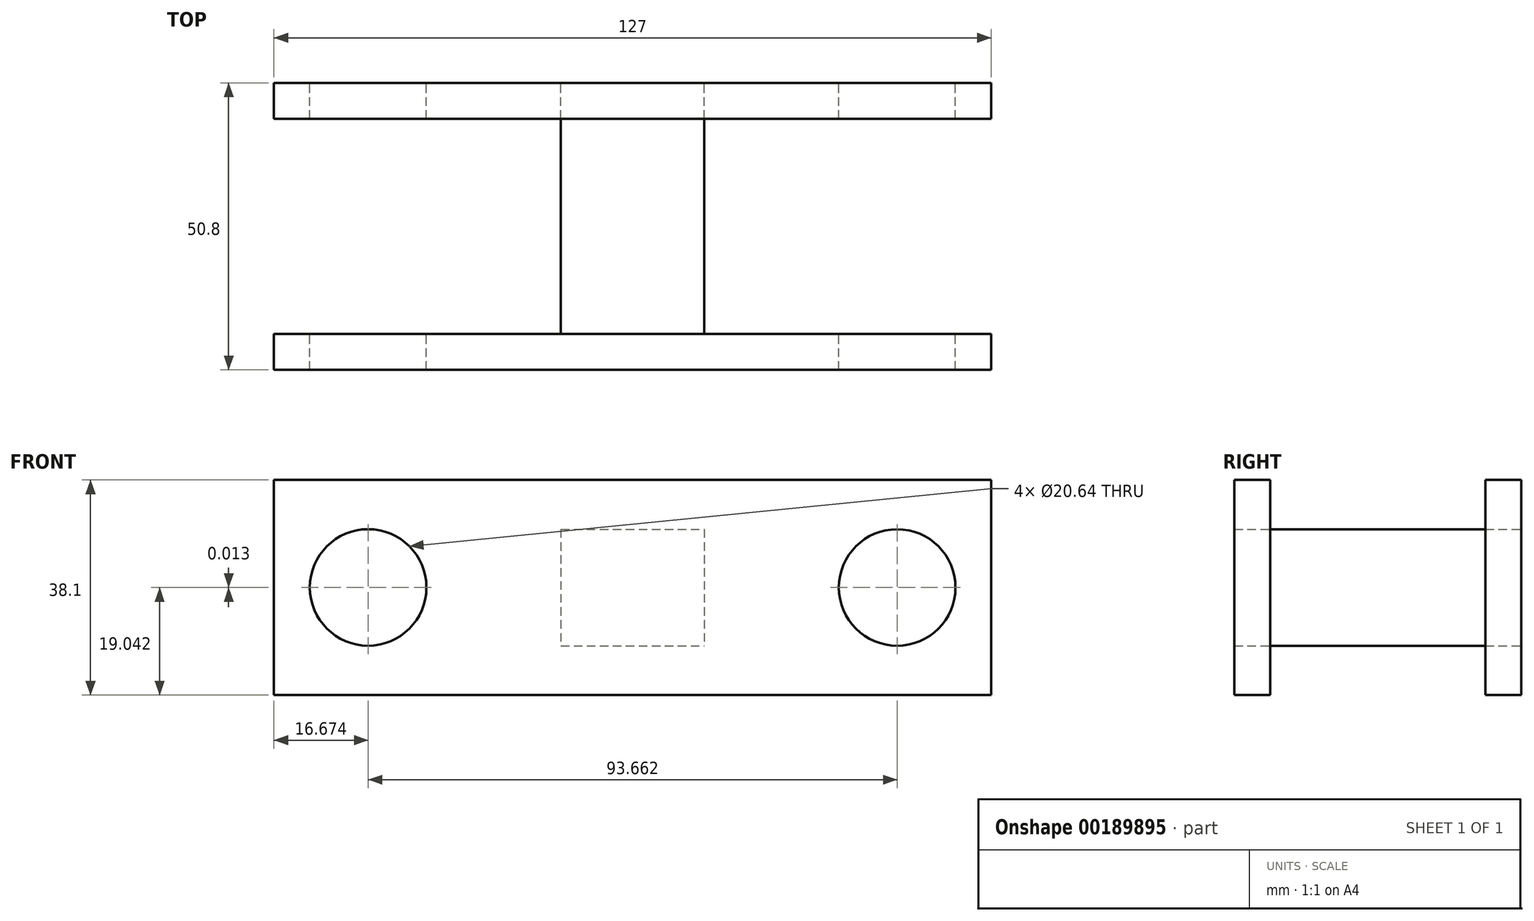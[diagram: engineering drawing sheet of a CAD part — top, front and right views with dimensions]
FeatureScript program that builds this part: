
annotation { "Feature Type Name" : "Feature", "Feature Type Description" : "" }
export const myFeature = defineFeature(function(context is Context, id is Id, definition is map)
    precondition{}
    {
        {
            var Q0;
            Q0=qCreatedBy(makeId("Front.planeOp"),FACE);
            var sketch = newSketch(context, id + "F0", { "sketchPlane" : qUnion([Q0])});
            skCircle(sketch, "E0", {"center": v(45.25, -0.5) * mm, "radius": 10.32 * mm});
            skLineSegment(sketch, "E1.bottom", {"start": v(-65.09, 18.55) * mm, "end": v(61.91, 18.55) * mm});
            skLineSegment(sketch, "E1.top", {"start": v(-65.09, -19.55) * mm, "end": v(61.91, -19.55) * mm});
            skLineSegment(sketch, "E1.left", {"start": v(-65.09, 18.55) * mm, "end": v(-65.09, -19.55) * mm});
            skLineSegment(sketch, "E1.right", {"start": v(61.91, 18.55) * mm, "end": v(61.91, -19.55) * mm});
            skCircle(sketch, "E2", {"center": v(-48.42, -0.5) * mm, "radius": 10.32 * mm});
            skLineSegment(sketch, "E3.bottom", {"start": v(-14.29, 9.81) * mm, "end": v(11.11, 9.81) * mm});
            skLineSegment(sketch, "E3.top", {"start": v(-14.29, -10.85) * mm, "end": v(11.11, -10.85) * mm});
            skLineSegment(sketch, "E3.left", {"start": v(-14.29, 9.81) * mm, "end": v(-14.29, -10.85) * mm});
            skLineSegment(sketch, "E3.right", {"start": v(11.11, 9.81) * mm, "end": v(11.11, -10.85) * mm});
            skSolve(sketch);
        }
        {
            var Q0;
            Q0=makeQuery(id+"F0.imprint","IMPRINT",FACE,{"disambiguationData":[TD([[makeQuery(id+"F0.imprint","IMPRINT",EDGE,{"derivedFrom":sQuery(id+"F0.wireOp",EDGE,"E0")}),-1.0]])]});
            var Q1;
            Q1=makeQuery(id+"F0.imprint","IMPRINT",FACE,{"disambiguationData":[TD([[makeQuery(id+"F0.imprint","IMPRINT",EDGE,{"derivedFrom":sQuery(id+"F0.wireOp",EDGE,"E3.bottom")}),-1.0]])]});
            extrude(context, id + "F1", {"entities" : qUnion([Q0, Q1]), "depth" : 6.35 * mm});
        }
        {
            var Q0;
            Q0=makeQuery(id+"F0.imprint","IMPRINT",FACE,{"disambiguationData":[TD([[makeQuery(id+"F0.imprint","IMPRINT",EDGE,{"derivedFrom":sQuery(id+"F0.wireOp",EDGE,"E3.bottom")}),-1.0]])]});
            extrude(context, id + "F2", {"entities" : qUnion([Q0]), "depth" : 44.45 * mm});
        }
        {
            var Q0;
            Q0=makeQuery(id+"F1.opExtrude","SWEPT_BODY",BODY,{"disambiguationData":[OSD([sQuery(id+"F0.wireOp",EDGE,"E0"),sQuery(id+"F0.wireOp",EDGE,"E1.bottom"),sQuery(id+"F0.wireOp",EDGE,"E1.top"),sQuery(id+"F0.wireOp",EDGE,"E1.left"),sQuery(id+"F0.wireOp",EDGE,"E1.right"),sQuery(id+"F0.wireOp",EDGE,"E2")])]});
            transform(context, id + "F3", {"entities" : qUnion([Q0]), "transformType" : TransformType.TRANSLATION_3D, "dx" : 0 * mm, "dy" : -44.45 * mm, "dz" : 0 * mm, "makeCopy" : true});
        }
    });
